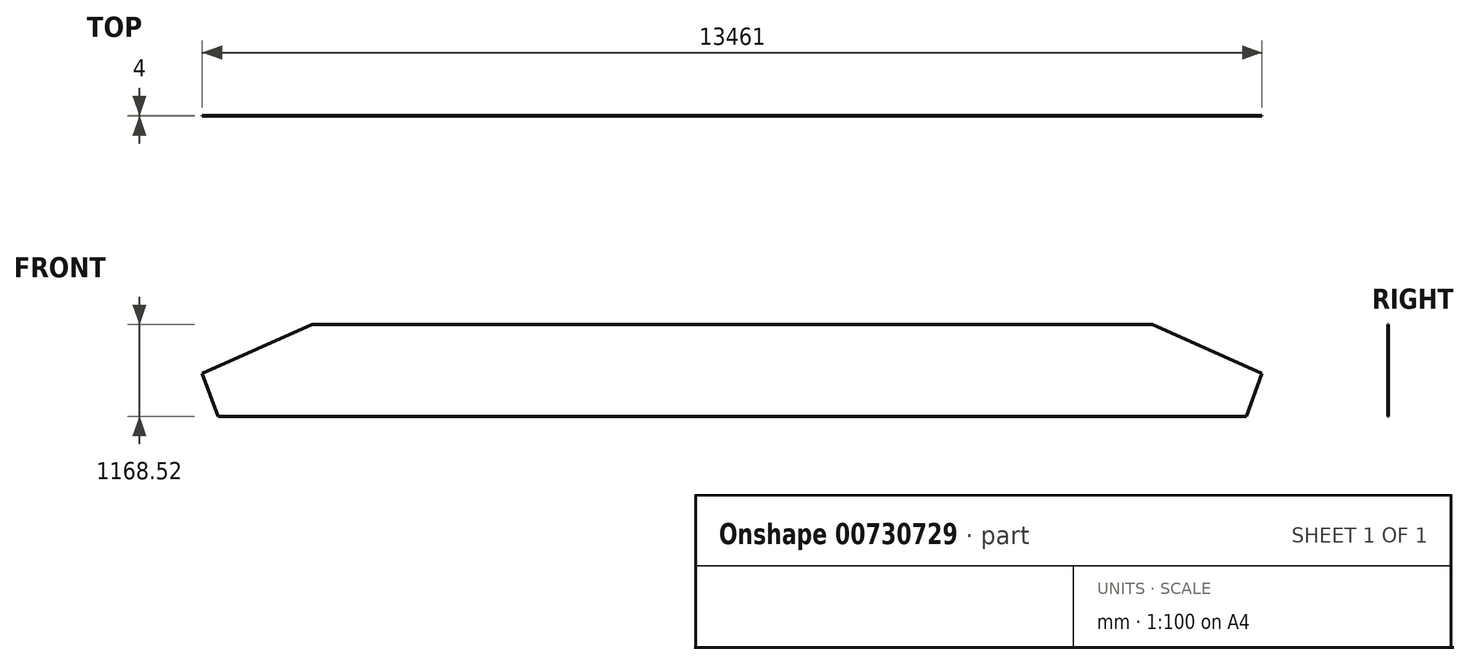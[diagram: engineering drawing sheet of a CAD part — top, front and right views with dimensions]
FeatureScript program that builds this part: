
annotation { "Feature Type Name" : "Feature", "Feature Type Description" : "" }
export const myFeature = defineFeature(function(context is Context, id is Id, definition is map)
    precondition{}
    {
        {
            var Q0;
            Q0=qCreatedBy(makeId("Front.planeOp"),FACE);
            var sketch = newSketch(context, id + "F0", { "sketchPlane" : qUnion([Q0])});
            skLineSegment(sketch, "E0", {"start": v(-6528.8, -584.26) * mm, "end": v(-6730.52, -38.47) * mm});
            skLineSegment(sketch, "E1", {"start": v(-6730.52, -38.47) * mm, "end": v(-5339.44, 584.26) * mm});
            skLineSegment(sketch, "E2", {"start": v(-5339.44, 584.26) * mm, "end": v(0, 584.26) * mm});
            skLineSegment(sketch, "E3", {"start": v(0, 584.26) * mm, "end": v(0, 457.26) * mm});
            skLineSegment(sketch, "E4", {"start": v(0, 457.26) * mm, "end": v(0, 584.26) * mm});
            skLineSegment(sketch, "E5", {"start": v(0, 584.26) * mm, "end": v(5339.41, 584.26) * mm});
            skLineSegment(sketch, "E6", {"start": v(5339.41, 584.26) * mm, "end": v(6730.52, -38.47) * mm});
            skLineSegment(sketch, "E7", {"start": v(6730.52, -38.47) * mm, "end": v(6528.8, -584.26) * mm});
            skLineSegment(sketch, "E8", {"start": v(6528.8, -584.26) * mm, "end": v(0, -584.26) * mm});
            skLineSegment(sketch, "E9", {"start": v(0, -584.26) * mm, "end": v(0, -457.26) * mm});
            skLineSegment(sketch, "E10", {"start": v(0, -457.26) * mm, "end": v(0, -584.26) * mm});
            skLineSegment(sketch, "E11", {"start": v(0, -584.26) * mm, "end": v(-6528.8, -584.26) * mm});
            skSolve(sketch);
        }
        {
            var Q0;
            Q0 = qSketchRegion(id + "F0", true);
            extrude(context, id + "F1", {"entities" : qUnion([Q0]), "depth" : 4 * mm, "offsetDistance" : 25 * mm});
        }
    });
